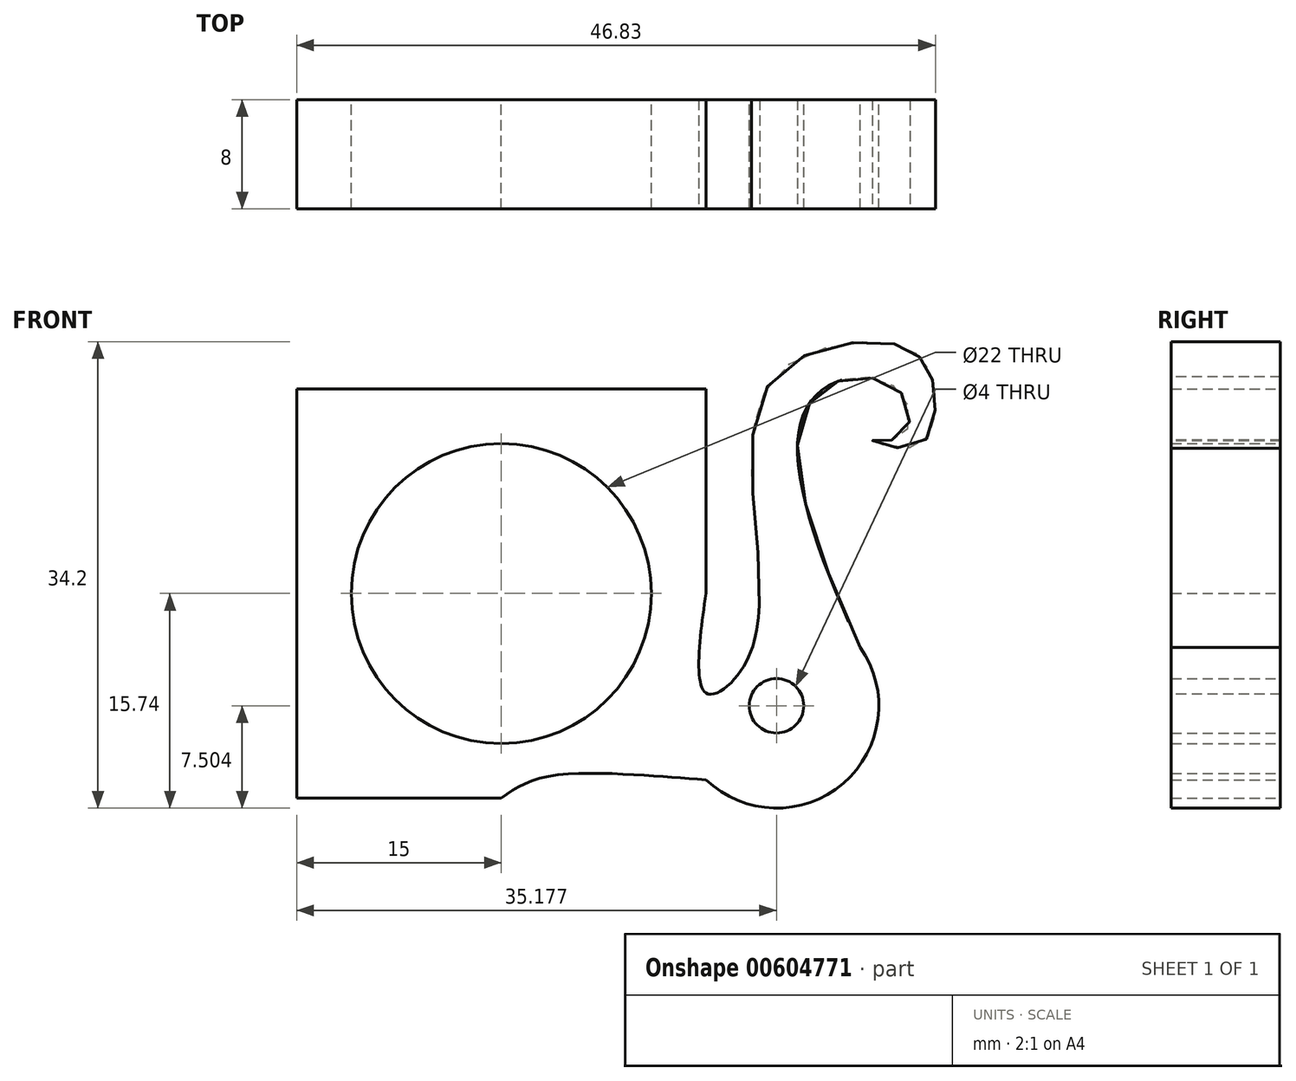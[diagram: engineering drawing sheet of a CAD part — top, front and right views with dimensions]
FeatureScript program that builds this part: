
annotation { "Feature Type Name" : "Feature", "Feature Type Description" : "" }
export const myFeature = defineFeature(function(context is Context, id is Id, definition is map)
    precondition{}
    {
        {
            var Q0;
            Q0=qCreatedBy(makeId("Front.planeOp"),FACE);
            var sketch = newSketch(context, id + "F0", { "sketchPlane" : qUnion([Q0])});
            skLineSegment(sketch, "E0.bottom", {"start": v(-15, 15) * mm, "end": v(15, 15) * mm});
            skLineSegment(sketch, "E0.top", {"start": v(-15, -15) * mm, "end": v(0, -15) * mm});
            skLineSegment(sketch, "E0.left", {"start": v(-15, 15) * mm, "end": v(-15, -15) * mm});
            skLineSegment(sketch, "E0.right", {"start": v(15, 15) * mm, "end": v(15, 0) * mm});
            skPoint(sketch, "E0.middle", {"position": v(0, 0) * mm});
            skPoint(sketch, "E1.center.orphan", {"position": v(-1.22, 0) * mm});
            skCircle(sketch, "E2", {"center": v(0, 0) * mm, "radius": 11 * mm});
            skFitSpline(sketch, "E3", {"points": [v(0, -15) * mm, v(3, -13.5) * mm, v(9.91, -13.3) * mm, v(15, -13.66) * mm], "startDerivative": vector(9.35, 6.5) * mm, "endDerivative": vector(14, -1.13) * mm});
            skPoint(sketch, "E4.orphan", {"position": v(15, -15) * mm});
            skArc(sketch, "E5", {"start": v(15, -13.66) * mm, "mid": v(27.35, -10.43) * mm, "end": v(18.92, -0.84) * mm});
            skPoint(sketch, "E5.second.point", {"position": v(27.36, -6.08) * mm});
            skPoint(sketch, "E5.third.point", {"position": v(26.8, -11.74) * mm});
            skCircle(sketch, "E6", {"center": v(20.18, -8.24) * mm, "radius": 2 * mm});
            skPoint(sketch, "E7.0.internal.snap0", {"position": v(15, 0.67) * mm});
            skFitSpline(sketch, "E7", {"points": [v(15, 0) * mm, v(15, -7.3) * mm, v(17.73, -5.42) * mm, v(18.8, 3.43) * mm, v(19.85, 15.65) * mm, v(28.2, 18.4) * mm, v(31.08, 16.84) * mm, v(31.82, 13.6) * mm, v(30.26, 10.73) * mm, v(27.2, 11.23) * mm, v(29.2, 11.41) * mm, v(29.58, 14.34) * mm, v(25.78, 15.84) * mm, v(21.9, 12.41) * mm, v(27.36, -6.08) * mm], "startDerivative": vector(-14.83, -105.5) * mm, "endDerivative": vector(75.42, -152.4) * mm});
            skLineSegment(sketch, "E8.trimOffspring", {"start": v(15, -7.3) * mm, "end": v(15, -13.66) * mm});
            skLineSegment(sketch, "E9", {"start": v(0, 0) * mm, "end": v(46.3, 46.14) * mm, "construction": true});
            skLineSegment(sketch, "E10", {"start": v(46.3, 46.14) * mm, "end": v(-25.96, -25.87) * mm, "construction": true});
            skSolve(sketch);
        }
        {
            var Q0;
            Q0 = qSketchRegion(id + "F0", true);
            extrude(context, id + "F1", {"entities" : qUnion([Q0]), "depth" : 8 * mm, "offsetDistance" : 25 * mm});
        }
    });
